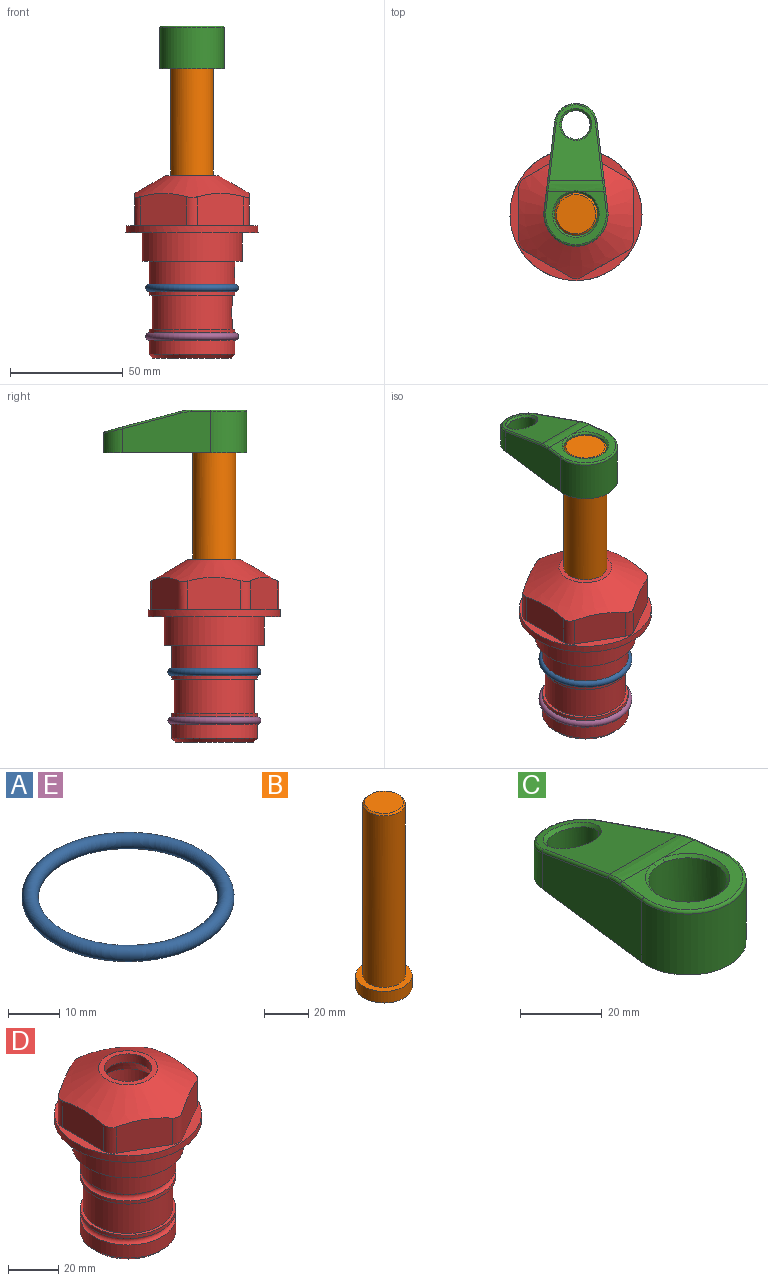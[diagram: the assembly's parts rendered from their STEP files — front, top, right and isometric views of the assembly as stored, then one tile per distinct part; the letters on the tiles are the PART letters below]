
ASSEMBLY  parts=5 mates=4
PART A: 1 faces, bbox 44.7x44.7x3.2 mm
  f0: torus R=19.05mm, axis (0,0,1), area 1193.9mm2
PART B: 6 faces, bbox 25.4x25.4x101.6 mm
  f0: plane 17.46x17.46mm, normal (0,0,1), area 239.5mm2, adj f5
  f1: plane 25.4x25.4mm, normal (0,0,-1), area 506.7mm2, adj f2
  f2: cylinder r=12.7mm len=25.4mm, axis (0,0,1), area 506.7mm2, adj f1,f3
  f3: plane 25.4x25.4mm, normal (0,0,1), area 221.7mm2, adj f2,f4
  f4: cylinder r=9.53mm len=94.46mm, axis (0,0,1), area 5653mm2, adj f3,f5
  f5: cone r=8.73mm half-angle=45deg, axis (0,0,-1), area 64.4mm2, adj f0,f4
PART C: 31 faces, bbox 31.7x65.5x19.8 mm
  f0: plane 39.12x18.26mm, normal (0.99,0.12,0), area 612.2mm2, adj f1,f4,f7,f11,f13,f15
  f1: cylinder r=9.53mm len=18.91mm, axis (0,0,-1), area 296.1mm2, adj f0,f2,f7,f17
  f2: plane 39.12x18.26mm, normal (-0.99,0.12,0), area 612.2mm2, adj f1,f4,f7,f12,f14,f16
  f3: cylinder r=6.35mm len=12.7mm, axis (0,0,-1), area 362.4mm2, adj f7,f18
  f4: cylinder r=14.29mm len=28.58mm, axis (0,0,-1), area 882.2mm2, adj f0,f2,f7,f10
  f5: cylinder r=9.53mm len=19.05mm, axis (0,0,-1), area 1092.6mm2, adj f7,f19,f20
  f6: plane 26.99x23.69mm, normal (0,0,1), area 216.2mm2, adj f9,f10,f11,f12,f19
  f7: plane 63.5x28.58mm, normal (0,0,-1), area 661.8mm2, adj f0,f1,f2,f3,f4,f5,f22,f23
  f8: plane 33.52x23.6mm, normal (0,0.26,0.97), area 486mm2, adj f9,f15,f16,f17,f18
  f9: cylinder r=19.05mm len=24.72mm, axis (1,0,0), area 120.4mm2, adj f6,f8,f13,f14,f20
  f10: torus R=13.49mm, axis (0,0,1), area 59mm2, adj f4,f6,f11,f12
  f11: cylinder r=0.79mm len=8.67mm, axis (0.12,-0.99,0), area 10.8mm2, adj f0,f6,f10,f13
  f12: cylinder r=0.79mm len=8.67mm, axis (0.12,0.99,0), area 10.8mm2, adj f2,f6,f10,f14
  f13: bspline ~4.95x1.42mm, area 6.1mm2, adj f0,f9,f11,f15
  f14: bspline ~4.95x1.42mm, area 6.1mm2, adj f2,f9,f12,f16
  f15: cylinder r=0.79mm len=25.95mm, axis (0.12,-0.96,0.26), area 32.9mm2, adj f0,f8,f13,f17
  f16: cylinder r=0.79mm len=25.95mm, axis (0.12,0.96,-0.26), area 32.9mm2, adj f2,f8,f14,f17
  f17: bspline ~18.91x8.38mm, area 30mm2, adj f1,f8,f15,f16
  f18: bspline ~14.29x14.29mm, area 48.3mm2, adj f3,f8
  f19: cone r=9.53mm half-angle=45deg, axis (0,0,1), area 66.5mm2, adj f5,f6,f20
  f20: bspline ~3.22x0.96mm, area 3.5mm2, adj f5,f9,f19
  f21: plane 2.75x2.72mm, normal (0,0,-1), area 2.9mm2, adj f23,f25,f28
  f22: plane 23.05x15.88mm, normal (-0.99,-0.12,0), area 323.6mm2, adj f7,f25,f26,f27,f28,f29
  f23: plane 23.05x15.88mm, normal (0.99,-0.12,0), area 323.6mm2, adj f7,f21,f25,f27,f28,f30
  f24: cylinder r=9.53mm len=10.69mm, axis (0,0,-1), area 114.7mm2, adj f7,f27,f29,f30
  f25: cylinder r=12.7mm len=20.59mm, axis (0,0,-1), area 381.1mm2, adj f7,f21,f22,f23,f26,f28
  f26: plane 2.75x2.72mm, normal (0,0,-1), area 2.9mm2, adj f22,f25,f28
  f27: plane 19.72x18.37mm, normal (0,-0.26,-0.97), area 291.8mm2, adj f22,f23,f24,f28,f29,f30
  f28: cylinder r=15.88mm len=19.92mm, axis (1,0,0), area 54.8mm2, adj f21,f22,f23,f25,f26,f27
  f29: cylinder r=1.59mm len=11mm, axis (0,0,-1), area 34.7mm2, adj f7,f22,f24,f27
  f30: cylinder r=1.59mm len=11mm, axis (0,0,-1), area 34.7mm2, adj f7,f23,f24,f27
PART D: 36 faces, bbox 58.7x58.7x81 mm
  f0: cylinder r=17.78mm len=35.56mm, axis (0,0,1), area 1670.8mm2, adj f23,f24,f31
  f1: cylinder r=19.05mm len=38.1mm, axis (0,0,1), area 1191.9mm2, adj f26,f27,f30
  f2: plane 58.66x58.66mm, normal (0,0,-1), area 1150.6mm2, adj f3,f28
  f3: cylinder r=29.33mm len=58.66mm, axis (0,0,-1), area 585.1mm2, adj f2,f4
  f4: plane 58.66x58.66mm, normal (0,0,1), area 475.9mm2, adj f3,f5,f6,f7,f8,f9,f10,f11
  f5: plane 20.32x14.34mm, normal (-0.5,0.87,0), area 324.4mm2, adj f4,f15,f16,f17
  f6: plane 20.32x14.34mm, normal (0.5,0.87,0), area 324.4mm2, adj f4,f14,f15,f17
  f7: plane 23.48x14.34mm, normal (1,0,0), area 324.4mm2, adj f4,f13,f14,f17
  f8: plane 20.32x14.34mm, normal (0.5,-0.87,0), area 324.4mm2, adj f4,f12,f13,f17
  f9: plane 20.32x14.34mm, normal (-0.5,-0.87,0), area 324.4mm2, adj f4,f11,f12,f17
  f10: plane 23.48x14.34mm, normal (-1,0,0), area 324.4mm2, adj f4,f11,f16,f17
  f11: cylinder r=5.08mm len=12.85mm, axis (0,0,-1), area 67.2mm2, adj f4,f9,f10,f17
  f12: cylinder r=5.08mm len=12.85mm, axis (0,0,-1), area 67.2mm2, adj f4,f8,f9,f17
  f13: cylinder r=5.08mm len=12.85mm, axis (0,0,-1), area 67.2mm2, adj f4,f7,f8,f17
  f14: cylinder r=5.08mm len=12.85mm, axis (0,0,-1), area 67.2mm2, adj f4,f6,f7,f17
  f15: cylinder r=5.08mm len=12.85mm, axis (0,0,-1), area 67.2mm2, adj f4,f5,f6,f17
  f16: cylinder r=5.08mm len=12.85mm, axis (0,0,-1), area 67.2mm2, adj f4,f5,f10,f17
  f17: cone r=11.73mm half-angle=60deg, axis (0,0,-1), area 2071.8mm2, adj f5,f6,f7,f8,f9,f10,f11,f12
  f18: plane 23.46x23.46mm, normal (0,0,1), area 147.4mm2, adj f17,f35
  f19: plane 34.93x34.93mm, normal (0,0,-1), area 958mm2, adj f29
  f20: cylinder r=19.05mm len=38.1mm, axis (0,0,1), area 760.1mm2, adj f21,f29
  f21: torus R=19.05mm, axis (0,0,1), area 565.3mm2, adj f20,f22
  f22: cylinder r=19.05mm len=38.1mm, axis (0,0,1), area 190mm2, adj f21,f23
  f23: plane 38.1x38.1mm, normal (0,0,1), area 146.9mm2, adj f0,f22
  f24: plane 38.1x38.1mm, normal (0,0,-1), area 146.9mm2, adj f0,f25
  f25: cylinder r=19.05mm len=38.1mm, axis (0,0,1), area 190mm2, adj f24,f26
  f26: torus R=19.05mm, axis (0,0,1), area 565.3mm2, adj f1,f25
  f27: plane 44.45x44.45mm, normal (0,0,-1), area 411.7mm2, adj f1,f28
  f28: cylinder r=22.23mm len=44.45mm, axis (0,0,1), area 1773.5mm2, adj f2,f27
  f29: cone r=19.05mm half-angle=45deg, axis (0,0,1), area 257.5mm2, adj f19,f20
  f30: cylinder r=3.17mm len=6.75mm, axis (-1,0,0), area 128mm2, adj f1,f33
  f31: cylinder r=3.17mm len=6.35mm, axis (-1,0,0), area 102.5mm2, adj f0,f33
  f32: plane 25.4x25.4mm, normal (0,0,1), area 506.7mm2, adj f33
  f33: cylinder r=12.7mm len=66.42mm, axis (0,0,-1), area 5236.2mm2, adj f30,f31,f32,f34
  f34: cone r=9.53mm half-angle=30deg, axis (0,0,-1), area 443.4mm2, adj f33,f35
  f35: cylinder r=9.53mm len=19.05mm, axis (0,0,-1), area 240.9mm2, adj f18,f34
PART E: same geometry as A
PLACE A at identity
PLACE B rot(axis=(0,0,1),0.1deg) t=(0,0,27.55)mm
PLACE C rot(axis=(0,0,1),0.1deg) t=(0,0,28.35)mm
PLACE D at identity fixed
PLACE E t=(0,0,-21.59)mm
MATE fastened E.f0 <-> D.f0  axis (0,0,1) through (0,0,-46.1)mm
MATE fastened A.f0 <-> D.f0  axis (0,0,1) through (0,0,-24.51)mm
MATE fastened B.f2 <-> C.f4  axis (0,0,1) through (0,0,91.05)mm
MATE cylindrical B.f2 <-> D.f0  axis (0,0,-1) through (0,0,-10.55)mm
